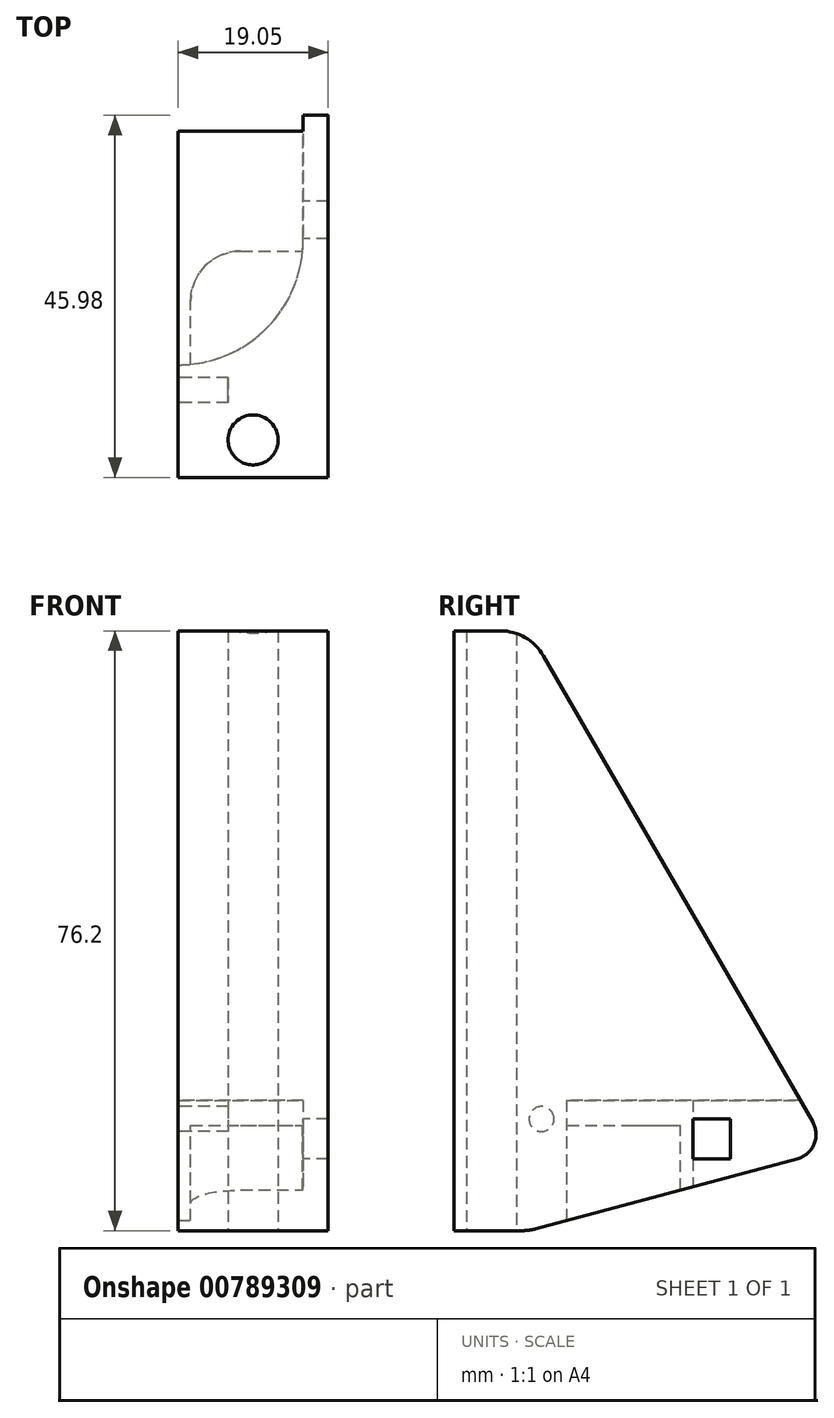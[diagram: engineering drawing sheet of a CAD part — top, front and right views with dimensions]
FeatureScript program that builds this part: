
annotation { "Feature Type Name" : "Feature", "Feature Type Description" : "" }
export const myFeature = defineFeature(function(context is Context, id is Id, definition is map)
    precondition{}
    {
        {
            var Q0;
            Q0=qCreatedBy(makeId("Right.planeOp"),FACE);
            var sketch = newSketch(context, id + "F0", { "sketchPlane" : qUnion([Q0])});
            skLineSegment(sketch, "E0", {"start": v(-2.07, 3.58) * mm, "end": v(-36.27, 62.82) * mm});
            skLineSegment(sketch, "E1", {"start": v(-37.3, -10) * mm, "end": v(-4, -1.07) * mm});
            skPoint(sketch, "E2.visualSharp", {"position": v(-38.1, 66) * mm});
            skPoint(sketch, "E3.visualSharp", {"position": v(0, 0) * mm});
            skArc(sketch, "E3.filletArc", {"start": v(-4, -1.07) * mm, "mid": v(-1.89, 0.78) * mm, "end": v(-2.07, 3.58) * mm});
            skPoint(sketch, "E4.visualSharp", {"position": v(-38.1, -10.2) * mm});
            skLineSegment(sketch, "E5", {"start": v(-41.77, 66) * mm, "end": v(-47.63, 66) * mm});
            skLineSegment(sketch, "E6", {"start": v(-38.94, -10.2) * mm, "end": v(-47.62, -10.2) * mm});
            skLineSegment(sketch, "E7", {"start": v(-47.62, -10.2) * mm, "end": v(-47.62, 66) * mm});
            skPoint(sketch, "E8.visualSharp", {"position": v(-38.1, 59.64) * mm});
            skPoint(sketch, "E9.visualSharp", {"position": v(-38.1, -3.86) * mm});
            skArc(sketch, "E10.filletArc", {"start": v(-38.94, -10.2) * mm, "mid": v(-38.1, -10.15) * mm, "end": v(-37.3, -10) * mm});
            skArc(sketch, "E11.filletArc", {"start": v(-36.27, 62.82) * mm, "mid": v(-38.6, 65.14) * mm, "end": v(-41.77, 66) * mm});
            skSolve(sketch);
        }
        {
            var Q0;
            Q0=qSketchRegion(id+"F0",true);
            extrude(context, id + "F1", {"entities" : qUnion([Q0]), "depth" : 19.05 * mm});
        }
        {
            var Q0;
            Q0=makeQuery(id+"F1.opExtrude","SWEPT_FACE",FACE,{"disambiguationData":[OSD([sQuery(id+"F0.wireOp",EDGE,"E6")])]});
            var sketch = newSketch(context, id + "F2", { "sketchPlane" : qUnion([Q0])});
            skLineSegment(sketch, "E12", {"start": v(9.53, 47.62) * mm, "end": v(9.53, 38.1) * mm, "construction": true});
            skPoint(sketch, "E13", {"position": v(9.53, 42.86) * mm});
            skSolve(sketch);
        }
        {
            var Q0;
            Q0=sQuery(id+"F2.wireOp",VERTEX,"E13");
            var Q1;
            Q1=makeQuery(id+"F1.opExtrude","SWEPT_BODY",BODY,{"disambiguationData":[OSD([sQuery(id+"F0.wireOp",EDGE,"E0"),sQuery(id+"F0.wireOp",EDGE,"E1"),sQuery(id+"F0.wireOp",EDGE,"E3.filletArc"),sQuery(id+"F0.wireOp",EDGE,"E5"),sQuery(id+"F0.wireOp",EDGE,"LSD3Qvf9-NvaC-n9SQ-XStv-JzqC34BARIO8"),sQuery(id+"F0.wireOp",EDGE,"q4ttR19L-JsQ6-2Oj6-suNv-tmyb9m5r0BPJ"),sQuery(id+"F0.wireOp",EDGE,"E6"),sQuery(id+"F0.wireOp",EDGE,"E7"),sQuery(id+"F0.wireOp",EDGE,"C7pJZ6hP-eq9H-iINe-mSxK-QcilfCuAnHeq"),sQuery(id+"F0.wireOp",EDGE,"y15EkDpz-Shtx-Dssd-Mlw5-IhtF37jcYgsN"),sQuery(id+"F0.wireOp",EDGE,"E8.filletArc"),sQuery(id+"F0.wireOp",EDGE,"E9.filletArc"),sQuery(id+"F0.wireOp",EDGE,"E10.filletArc"),sQuery(id+"F0.wireOp",EDGE,"E11.filletArc")])]});
            hole(context, id + "F3", {"style" : HoleStyle.SIMPLE, "endStyle" : HoleEndStyle.THROUGH, "holeDiameter" : 6.35 * mm, "isTappedThrough" : true, "tappedDepth" : 12.7 * mm, "tapClearance" : 3, "locations" : qUnion([Q0]), "scope" : qUnion([Q1])});
        }
        {
            var Q0;
            Q0=qCreatedBy(makeId("Top.planeOp"),FACE);
            var sketch = newSketch(context, id + "F4", { "sketchPlane" : qUnion([Q0])});
            skArc(sketch, "E14", {"start": v(0, -1.59) * mm, "mid": v(-11.16, -28.75) * mm, "end": v(15.87, -17.29) * mm});
            skLineSegment(sketch, "E15", {"start": v(0, -1.59) * mm, "end": v(15.87, -1.59) * mm});
            skLineSegment(sketch, "E16", {"start": v(15.87, -17.29) * mm, "end": v(15.87, -10.96) * mm});
            skLineSegment(sketch, "E17", {"start": v(15.87, -10.96) * mm, "end": v(15.87, -1.59) * mm});
            skSolve(sketch);
        }
        {
            var Q0;
            Q0 = qSketchRegion(id + "F4", true);
            extrude(context, id + "F5", {"entities" : qUnion([Q0]), "operationType" : NewBodyOperationType.REMOVE, "depth" : 6.35 * mm, "offsetDistance" : 25.4 * mm, "hasSecondDirection" : true, "secondDirectionBound" : SecondDirectionBoundingType.THROUGH_ALL, "secondDirectionOppositeDirection" : true, "secondDirectionDepth" : 25.4 * mm});
        }
        {
            var Q0;
            Q0=makeQuery(id+"F5.boolean.opBoolean","COPY",FACE,{"derivedFrom":makeQuery(id+"F5.opExtrude","SWEPT_FACE",FACE,{"disambiguationData":[OSD([sQuery(id+"F4.wireOp",EDGE,"E16"),sQuery(id+"F4.wireOp",EDGE,"E17")])]})});
            var sketch = newSketch(context, id + "F6", { "sketchPlane" : qUnion([Q0])});
            skLineSegment(sketch, "E18.bottom", {"start": v(17.29, -1.11) * mm, "end": v(12.52, -1.11) * mm});
            skLineSegment(sketch, "E18.top", {"start": v(17.29, 3.97) * mm, "end": v(12.52, 3.97) * mm});
            skLineSegment(sketch, "E18.left", {"start": v(17.29, -1.11) * mm, "end": v(17.29, 3.97) * mm});
            skLineSegment(sketch, "E18.right", {"start": v(12.52, -1.11) * mm, "end": v(12.52, 3.97) * mm});
            skSolve(sketch);
        }
        {
            var Q0;
            Q0 = qSketchRegion(id + "F6", true);
            extrude(context, id + "F7", {"entities" : qUnion([Q0]), "operationType" : NewBodyOperationType.REMOVE, "oppositeDirection" : true, "depth" : 25.4 * mm, "offsetDistance" : 25.4 * mm});
        }
        {
            var Q0;
            Q0=makeQuery(id+"F1.opExtrude","CAP_FACE",FACE,{"disambiguationData":[OSD([sQuery(id+"F0.wireOp",EDGE,"E0"),sQuery(id+"F0.wireOp",EDGE,"E1"),sQuery(id+"F0.wireOp",EDGE,"E3.filletArc"),sQuery(id+"F0.wireOp",EDGE,"E5"),sQuery(id+"F0.wireOp",EDGE,"E6"),sQuery(id+"F0.wireOp",EDGE,"E7"),sQuery(id+"F0.wireOp",EDGE,"E10.filletArc"),sQuery(id+"F0.wireOp",EDGE,"E11.filletArc")])],"isStart":true});
            var sketch = newSketch(context, id + "F8", { "sketchPlane" : qUnion([Q0])});
            skCircle(sketch, "E19", {"center": v(36.51, 3.97) * mm, "radius": 1.59 * mm});
            skSolve(sketch);
        }
        {
            var Q0;
            Q0 = qSketchRegion(id + "F8", true);
            extrude(context, id + "F9", {"entities" : qUnion([Q0]), "operationType" : NewBodyOperationType.REMOVE, "oppositeDirection" : true, "depth" : 6.35 * mm, "offsetDistance" : 25.4 * mm});
        }
        {
            var Q0;
            Q0=makeQuery(id+"F5.boolean.opBoolean","COPY",FACE,{"derivedFrom":makeQuery(id+"F5.opExtrude","CAP_FACE",FACE,{"disambiguationData":[OSD([sQuery(id+"F4.wireOp",EDGE,"E14"),sQuery(id+"F4.wireOp",EDGE,"E15"),sQuery(id+"F4.wireOp",EDGE,"E16"),sQuery(id+"F4.wireOp",EDGE,"E17")])],"isStart":false})});
            var sketch = newSketch(context, id + "F10", { "sketchPlane" : qUnion([Q0])});
            skLineSegment(sketch, "E20.0", {"start": v(7.94, 18.87) * mm, "end": v(15.87, 18.87) * mm});
            skLineSegment(sketch, "E20.1", {"start": v(1.59, 33.34) * mm, "end": v(1.59, 25.22) * mm});
            skPoint(sketch, "E21.visualSharp", {"position": v(1.59, 18.87) * mm});
            skArc(sketch, "E21.filletArc", {"start": v(1.59, 25.22) * mm, "mid": v(3.45, 20.73) * mm, "end": v(7.94, 18.87) * mm});
            skSolve(sketch);
        }
        {
            var Q0;
            Q0 = qSketchRegion(id + "F10", true);
            var Q1;
            {var subQ0=sQuery(id+"F10.wireOp",EDGE,"E21.filletArc");Q1=makeQuery(id+"F10.imprint","IMPRINT",FACE,{"disambiguationData":[TD([[makeQuery(id+"F10.imprint","IMPRINT",EDGE,{"derivedFrom":subQ0}),1.0]])]});}
            extrude(context, id + "F11", {"entities" : qUnion([Q0, Q1]), "operationType" : NewBodyOperationType.ADD, "depth" : 19.05 * mm, "offsetDistance" : 25.4 * mm, "hasSecondDirection" : true, "secondDirectionOppositeDirection" : true, "secondDirectionDepth" : -3.17 * mm});
        }
        {
            var Q0;
            Q0=makeQuery(id+"F1.opExtrude","CAP_FACE",FACE,{"disambiguationData":[OSD([sQuery(id+"F0.wireOp",EDGE,"E0"),sQuery(id+"F0.wireOp",EDGE,"E1"),sQuery(id+"F0.wireOp",EDGE,"E3.filletArc"),sQuery(id+"F0.wireOp",EDGE,"E5"),sQuery(id+"F0.wireOp",EDGE,"E6"),sQuery(id+"F0.wireOp",EDGE,"E7"),sQuery(id+"F0.wireOp",EDGE,"E10.filletArc"),sQuery(id+"F0.wireOp",EDGE,"E11.filletArc")])],"isStart":false});
            var sketch = newSketch(context, id + "F12", { "sketchPlane" : qUnion([Q0])});
            skLineSegment(sketch, "E22", {"start": v(-34.97, -9.37) * mm, "end": v(-14.9, -4) * mm});
            skLineSegment(sketch, "E23", {"start": v(-14.9, -4) * mm, "end": v(-14.9, -17.25) * mm});
            skLineSegment(sketch, "E24", {"start": v(-14.9, -17.25) * mm, "end": v(-35.4, -17.25) * mm});
            skLineSegment(sketch, "E25", {"start": v(-35.4, -17.25) * mm, "end": v(-34.97, -9.37) * mm});
            skSolve(sketch);
        }
        {
            var Q0;
            Q0=makeQuery(id+"F12.imprint","IMPRINT",FACE,{"disambiguationData":[TD([[makeQuery(id+"F12.imprint","IMPRINT",EDGE,{"derivedFrom":sQuery(id+"F12.wireOp",EDGE,"E22")}),-1.0]])]});
            extrude(context, id + "F13", {"entities" : qUnion([Q0]), "operationType" : NewBodyOperationType.REMOVE, "endBound" : BoundingType.THROUGH_ALL, "oppositeDirection" : true, "depth" : 25.4 * mm, "offsetDistance" : 25.4 * mm});
        }
    });
